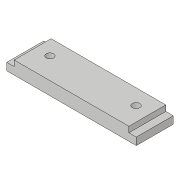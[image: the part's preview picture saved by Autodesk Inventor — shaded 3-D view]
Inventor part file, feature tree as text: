
AUTODESK INVENTOR PART (.ipt)
format: ipt  version: 2018.3 (Build 223284000, 284)  size: 138,752 bytes
history: native  units: in
note: dims shown in document units (in); Inventor stores cm internally (conversion verified against a paired STEP export)
features: extrude x3, sketch x3
ambient origin geometry x8: Origin, YZ Plane, XZ Plane, XY Plane, X Axis, Y Axis, Z Axis, Center Point
bodies: Solid1 (feature_tree)
feature tree (6):
  extrude  "Extrusion1"  Depth=0.625in
  extrude  "Extrusion6"  Depth=0.221in
  extrude  "Extrusion7"  Depth=0.096in
  sketch  "Sketch1"  dims[d0=2.1903in d1=0.625in]
  sketch  "Sketch7"  dims[d2=0.221in d3=0.0in d22=0.126in]
  sketch  "Sketch8"  dims[d23=0.126in d24=1.4567in d32=1.0in d33=0.0in d34=0.125in d35=0.125in d36=0.096in d37=0.0in d43=0.2619in d44=0.2619in d48=0.367in d49=0.3666in]
